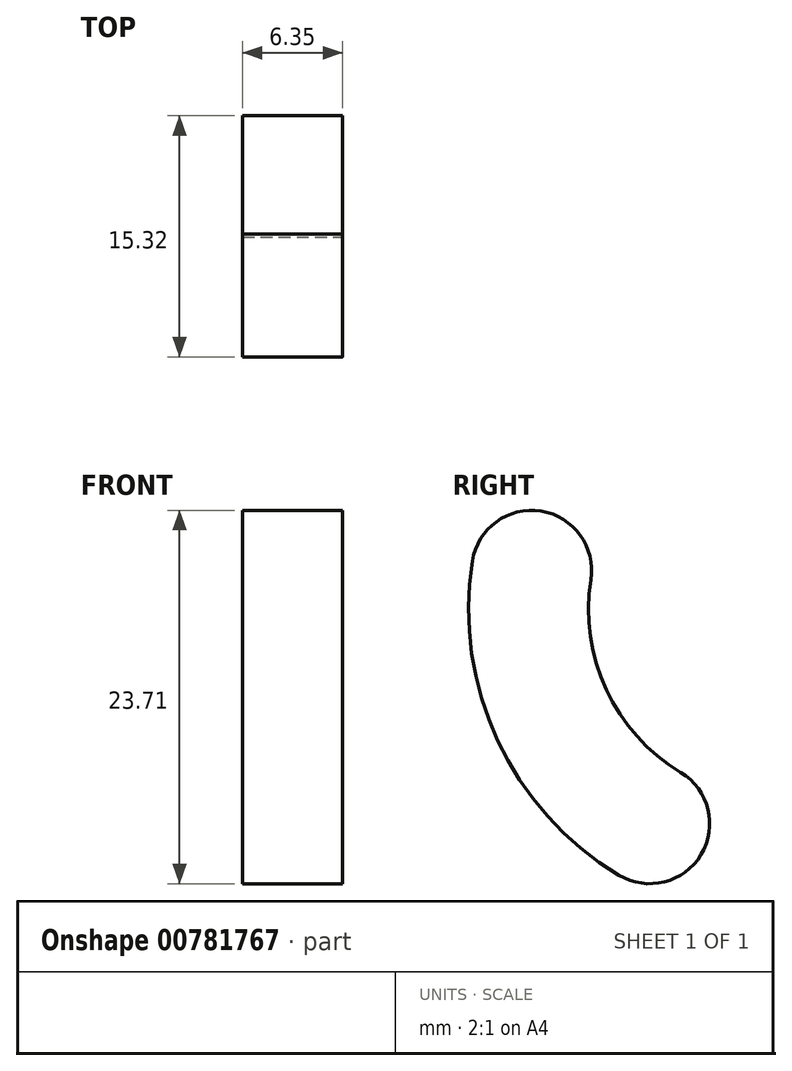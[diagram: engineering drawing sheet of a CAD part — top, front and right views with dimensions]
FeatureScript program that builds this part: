
annotation { "Feature Type Name" : "Feature", "Feature Type Description" : "" }
export const myFeature = defineFeature(function(context is Context, id is Id, definition is map)
    precondition{}
    {
        {
            var Q0;
            Q0=qCreatedBy(makeId("Top.planeOp"),FACE);
            var sketch = newSketch(context, id + "F0", { "sketchPlane" : qUnion([Q0])});
            skLineSegment(sketch, "E0.bottom", {"start": v(31.75, -31.75) * mm, "end": v(-31.75, -31.75) * mm});
            skLineSegment(sketch, "E0.top", {"start": v(31.75, 31.75) * mm, "end": v(-31.75, 31.75) * mm});
            skLineSegment(sketch, "E0.left", {"start": v(31.75, -31.75) * mm, "end": v(31.75, 31.75) * mm});
            skLineSegment(sketch, "E0.right", {"start": v(-31.75, -31.75) * mm, "end": v(-31.75, 31.75) * mm});
            skPoint(sketch, "E0.middle", {"position": v(0, 0) * mm});
            skLineSegment(sketch, "E1.bottom", {"start": v(25.4, -25.4) * mm, "end": v(-25.4, -25.4) * mm});
            skLineSegment(sketch, "E1.top", {"start": v(25.4, 25.4) * mm, "end": v(-25.4, 25.4) * mm});
            skLineSegment(sketch, "E1.left", {"start": v(25.4, -25.4) * mm, "end": v(25.4, 25.4) * mm});
            skLineSegment(sketch, "E1.right", {"start": v(-25.4, -25.4) * mm, "end": v(-25.4, 25.4) * mm});
            skSolve(sketch);
        }
        {
            var Q0;
            Q0=makeQuery(id+"F0.imprint","IMPRINT",FACE,{"disambiguationData":[TD([[makeQuery(id+"F0.imprint","IMPRINT",EDGE,{"derivedFrom":sQuery(id+"F0.wireOp",EDGE,"E0.bottom")}),-1.0]])]});
            extrude(context, id + "F1", {"entities" : qUnion([Q0]), "endBound" : BoundingType.SYMMETRIC, "depth" : 330.2 * mm, "offsetDistance" : 25.4 * mm});
        }
        {
            var Q0;
            Q0=makeQuery(id+"F1.opExtrude","SWEPT_FACE",FACE,{"disambiguationData":[OSD([sQuery(id+"F0.wireOp",EDGE,"E0.right")])]});
            var sketch = newSketch(context, id + "F2", { "sketchPlane" : qUnion([Q0])});
            skSolve(sketch);
        }
        {
            var Q0;
            Q0=makeQuery(id+"F1.opExtrude","SWEPT_FACE",FACE,{"disambiguationData":[OSD([sQuery(id+"F0.wireOp",EDGE,"E0.left")])]});
            var sketch = newSketch(context, id + "F3", { "sketchPlane" : qUnion([Q0])});
            skLineSegment(sketch, "E2.0", {"start": v(-31.75, 165.1) * mm, "end": v(31.75, 165.1) * mm, "construction": true});
            skLineSegment(sketch, "E2.1", {"start": v(-31.75, 165.1) * mm, "end": v(-31.75, -165.1) * mm, "construction": true});
            skLineSegment(sketch, "E2.2", {"start": v(31.75, 165.1) * mm, "end": v(31.75, -165.1) * mm, "construction": true});
            skLineSegment(sketch, "E2.3", {"start": v(-31.75, -165.1) * mm, "end": v(31.75, -165.1) * mm, "construction": true});
            skCircle(sketch, "E3", {"center": v(0, 146.05) * mm, "radius": 6.48 * mm});
            skArc(sketch, "E4", {"start": v(17.84, 137.73) * mm, "mid": v(19.5, 143.31) * mm, "end": v(19.44, 149.13) * mm});
            skArc(sketch, "E5", {"start": v(10.93, 140.95) * mm, "mid": v(11.95, 144.37) * mm, "end": v(11.92, 147.94) * mm});
            skLineSegment(sketch, "E6", {"start": v(0, 146.05) * mm, "end": v(19.44, 149.13) * mm, "construction": true});
            skLineSegment(sketch, "E7", {"start": v(0, 146.05) * mm, "end": v(9.54, 128.83) * mm, "construction": true});
            skLineSegment(sketch, "E8", {"start": v(0, 146.05) * mm, "end": v(24.19, 134.77) * mm, "construction": true});
            skCircle(sketch, "E9", {"center": v(0, 146.05) * mm, "radius": 15.88 * mm, "construction": true});
            skArc(sketch, "E10", {"start": v(11.92, 147.94) * mm, "mid": v(15.08, 152.3) * mm, "end": v(19.44, 149.13) * mm});
            skArc(sketch, "E11.MirrorCS", {"start": v(6.21, 135.7) * mm, "mid": v(4.91, 130.48) * mm, "end": v(10.14, 129.18) * mm});
            skArc(sketch, "E12.MirrorCS", {"start": v(10.93, 140.95) * mm, "mid": v(8.97, 137.98) * mm, "end": v(6.21, 135.7) * mm});
            skArc(sketch, "E13.MirrorCS", {"start": v(17.84, 137.73) * mm, "mid": v(14.63, 132.88) * mm, "end": v(10.14, 129.18) * mm});
            skLineSegment(sketch, "E14", {"start": v(0, 146.05) * mm, "end": v(-19.11, 146.05) * mm, "construction": true});
            skLineSegment(sketch, "E15", {"start": v(0, 146.05) * mm, "end": v(0, 119.4) * mm, "construction": true});
            skArc(sketch, "E16.MirrorCS", {"start": v(-6.21, 135.7) * mm, "mid": v(-4.91, 130.48) * mm, "end": v(-10.14, 129.18) * mm});
            skArc(sketch, "E17.MirrorCS", {"start": v(-17.84, 137.73) * mm, "mid": v(-14.63, 132.88) * mm, "end": v(-10.14, 129.18) * mm});
            skArc(sketch, "E18.MirrorCS", {"start": v(-17.84, 137.73) * mm, "mid": v(-19.5, 143.31) * mm, "end": v(-19.44, 149.13) * mm});
            skArc(sketch, "E19.MirrorCS", {"start": v(-11.92, 147.94) * mm, "mid": v(-15.08, 152.3) * mm, "end": v(-19.44, 149.13) * mm});
            skArc(sketch, "E20.MirrorCS", {"start": v(-10.93, 140.95) * mm, "mid": v(-11.95, 144.37) * mm, "end": v(-11.92, 147.94) * mm});
            skArc(sketch, "E21.MirrorCS", {"start": v(-10.93, 140.95) * mm, "mid": v(-8.97, 137.98) * mm, "end": v(-6.21, 135.7) * mm});
            skSolve(sketch);
        }
        {
            var Q0;
            Q0=makeQuery(id+"F3.imprint","IMPRINT",FACE,{"disambiguationData":[TD([[makeQuery(id+"F3.imprint","IMPRINT",EDGE,{"derivedFrom":sQuery(id+"F3.wireOp",EDGE,"E3")}),1.0]])]});
            var Q1;
            Q1=makeQuery(id+"F3.imprint","IMPRINT",FACE,{"disambiguationData":[TD([[makeQuery(id+"F3.imprint","IMPRINT",EDGE,{"derivedFrom":sQuery(id+"F3.wireOp",EDGE,"E4")}),1.0]])]});
            var Q2;
            Q2=makeQuery(id+"F3.imprint","IMPRINT",FACE,{"disambiguationData":[TD([[makeQuery(id+"F3.imprint","IMPRINT",EDGE,{"derivedFrom":sQuery(id+"F3.wireOp",EDGE,"E16.MirrorCS")}),-1.0]])]});
            extrude(context, id + "F4", {"entities" : qUnion([Q0, Q1, Q2]), "operationType" : NewBodyOperationType.REMOVE, "oppositeDirection" : true, "depth" : 25.4 * mm, "offsetDistance" : 25.4 * mm});
        }
        {
            var Q0;
            {var subQ0=sQuery(id+"F0.wireOp",EDGE,"E0.right");Q0=makeQuery(id+"F2.imprint","IMPRINT",FACE,{"disambiguationData":[TD([[makeQuery(id+"F2.imprint","IMPRINT",EDGE,{"derivedFrom":makeQuery(id+"F1.opExtrude","CAP_EDGE",EDGE,{"disambiguationData":[OSD([subQ0])],"isStart":true})}),-1.0]])]});}
            var sketch = newSketch(context, id + "F5", { "sketchPlane" : qUnion([Q0])});
            skCircle(sketch, "E22.0", {"center": v(0, 146.05) * mm, "radius": 6.48 * mm});
            skCircle(sketch, "E23", {"center": v(-7.7, 132.17) * mm, "radius": 1.9 * mm});
            skArc(sketch, "E24", {"start": v(5.1, 127.04) * mm, "mid": v(17.84, 137.73) * mm, "end": v(17.84, 154.37) * mm});
            skCircle(sketch, "E25", {"center": v(0, 146.05) * mm, "radius": 15.88 * mm, "construction": true});
            skLineSegment(sketch, "E26", {"start": v(0, 146.05) * mm, "end": v(5.1, 127.04) * mm, "construction": true});
            skLineSegment(sketch, "E27", {"start": v(0, 146.05) * mm, "end": v(-15.88, 146.05) * mm, "construction": true});
            skLineSegment(sketch, "E28", {"start": v(0, 146.05) * mm, "end": v(17.84, 154.37) * mm, "construction": true});
            skArc(sketch, "E29", {"start": v(3.12, 134.4) * mm, "mid": v(10.93, 140.95) * mm, "end": v(10.93, 151.15) * mm});
            skLineSegment(sketch, "E30", {"start": v(0, 146.05) * mm, "end": v(-7.7, 132.17) * mm});
            skArc(sketch, "E31", {"start": v(3.12, 134.4) * mm, "mid": v(0.43, 129.73) * mm, "end": v(5.1, 127.04) * mm});
            skArc(sketch, "E32", {"start": v(17.84, 154.37) * mm, "mid": v(12.78, 156.21) * mm, "end": v(10.93, 151.15) * mm});
            skCircle(sketch, "E33", {"center": v(-7.7, 132.17) * mm, "radius": 3.18 * mm, "construction": true});
            skLineSegment(sketch, "E34", {"start": v(0, 146.05) * mm, "end": v(-15.58, 149.08) * mm, "construction": true});
            skCircle(sketch, "E35", {"center": v(-15.58, 149.08) * mm, "radius": 3.18 * mm, "construction": true});
            skArc(sketch, "E36.0", {"start": v(-11.92, 147.94) * mm, "mid": v(-15.08, 152.3) * mm, "end": v(-19.44, 149.13) * mm, "construction": true});
            skLineSegment(sketch, "E37", {"start": v(0, 146.05) * mm, "end": v(-15.68, 148.53) * mm, "construction": true});
            skSolve(sketch);
        }
        {
            var Q0;
            Q0=qSketchRegion(id+"F5",true);
            extrude(context, id + "F6", {"entities" : qUnion([Q0]), "operationType" : NewBodyOperationType.REMOVE, "oppositeDirection" : true, "depth" : 25.4 * mm, "offsetDistance" : 25.4 * mm});
        }
        {
            var Q0;
            Q0=makeQuery(id+"F1.opExtrude","SWEPT_FACE",FACE,{"disambiguationData":[OSD([sQuery(id+"F0.wireOp",EDGE,"E0.left")])]});
            var sketch = newSketch(context, id + "F7", { "sketchPlane" : qUnion([Q0])});
            skArc(sketch, "E38", {"start": v(-8.89, 101.6) * mm, "mid": v(10.16, 82.55) * mm, "end": v(-8.89, 63.5) * mm, "construction": true});
            skArc(sketch, "E39.0", {"start": v(-8.89, 95.25) * mm, "mid": v(3.81, 82.55) * mm, "end": v(-8.89, 69.85) * mm});
            skArc(sketch, "E40.0", {"start": v(-8.89, 107.95) * mm, "mid": v(16.5, 82.55) * mm, "end": v(-8.89, 57.15) * mm});
            skArc(sketch, "E41", {"start": v(-8.89, 107.95) * mm, "mid": v(-15.24, 101.6) * mm, "end": v(-8.89, 95.25) * mm});
            skArc(sketch, "E42", {"start": v(-8.89, 57.15) * mm, "mid": v(-15.24, 63.5) * mm, "end": v(-8.89, 69.85) * mm});
            skArc(sketch, "E43", {"start": v(8.9, 6.35) * mm, "mid": v(-10.16, 25.4) * mm, "end": v(8.9, 44.45) * mm, "construction": true});
            skArc(sketch, "E44.0", {"start": v(8.9, 12.7) * mm, "mid": v(-3.8, 25.4) * mm, "end": v(8.9, 38.1) * mm});
            skArc(sketch, "E45.0", {"start": v(8.9, 0) * mm, "mid": v(-16.5, 25.4) * mm, "end": v(8.89, 50.8) * mm});
            skArc(sketch, "E46", {"start": v(8.9, 0) * mm, "mid": v(15.24, 6.35) * mm, "end": v(8.9, 12.7) * mm});
            skArc(sketch, "E47", {"start": v(8.9, 50.8) * mm, "mid": v(15.24, 44.45) * mm, "end": v(8.9, 38.1) * mm});
            skArc(sketch, "E48", {"start": v(-8.89, -12.7) * mm, "mid": v(10.16, -31.75) * mm, "end": v(-8.89, -50.8) * mm, "construction": true});
            skArc(sketch, "E49.0", {"start": v(-8.89, -19.05) * mm, "mid": v(3.81, -31.75) * mm, "end": v(-8.89, -44.45) * mm});
            skArc(sketch, "E50.0", {"start": v(-8.89, -6.35) * mm, "mid": v(16.5, -31.75) * mm, "end": v(-8.89, -57.15) * mm});
            skArc(sketch, "E51", {"start": v(-8.89, -6.35) * mm, "mid": v(-15.24, -12.7) * mm, "end": v(-8.89, -19.05) * mm});
            skArc(sketch, "E52", {"start": v(-8.89, -57.15) * mm, "mid": v(-15.24, -50.8) * mm, "end": v(-8.89, -44.45) * mm});
            skArc(sketch, "E53", {"start": v(8.9, -107.95) * mm, "mid": v(-10.16, -88.9) * mm, "end": v(8.89, -69.85) * mm, "construction": true});
            skArc(sketch, "E54.0", {"start": v(8.9, -101.6) * mm, "mid": v(-3.8, -88.9) * mm, "end": v(8.89, -76.2) * mm});
            skArc(sketch, "E55.0", {"start": v(8.9, -114.3) * mm, "mid": v(-16.5, -88.9) * mm, "end": v(8.89, -63.5) * mm});
            skArc(sketch, "E56", {"start": v(8.9, -114.3) * mm, "mid": v(15.24, -107.95) * mm, "end": v(8.9, -101.6) * mm});
            skArc(sketch, "E57", {"start": v(8.89, -63.5) * mm, "mid": v(15.24, -69.85) * mm, "end": v(8.89, -76.2) * mm});
            skCircle(sketch, "E58", {"center": v(-8.89, 82.55) * mm, "radius": 6.35 * mm});
            skCircle(sketch, "E59", {"center": v(8.9, 25.4) * mm, "radius": 6.35 * mm});
            skCircle(sketch, "E60", {"center": v(8.9, -88.9) * mm, "radius": 6.35 * mm});
            skCircle(sketch, "E61", {"center": v(-8.89, -31.75) * mm, "radius": 6.35 * mm});
            skSolve(sketch);
        }
        {
            var Q0;
            Q0=qSketchRegion(id+"F7",true);
            extrude(context, id + "F8", {"entities" : qUnion([Q0]), "operationType" : NewBodyOperationType.REMOVE, "endBound" : BoundingType.THROUGH_ALL, "oppositeDirection" : true, "depth" : 25.4 * mm, "offsetDistance" : 25.4 * mm});
        }
        {
            var Q0;
            Q0=makeQuery(id+"F1.opExtrude","SWEPT_FACE",FACE,{"disambiguationData":[OSD([sQuery(id+"F0.wireOp",EDGE,"E1.left")])]});
            var sketch = newSketch(context, id + "F9", { "sketchPlane" : qUnion([Q0])});
            skLineSegment(sketch, "E62.bottom", {"start": v(-25.4, 165.1) * mm, "end": v(25.4, 165.1) * mm});
            skLineSegment(sketch, "E62.top", {"start": v(-25.4, -127) * mm, "end": v(25.4, -127) * mm});
            skLineSegment(sketch, "E62.left", {"start": v(-25.4, 165.1) * mm, "end": v(-25.4, -127) * mm});
            skLineSegment(sketch, "E62.right", {"start": v(25.4, 165.1) * mm, "end": v(25.4, -127) * mm});
            skLineSegment(sketch, "E63.bottom", {"start": v(46.54, -190) * mm, "end": v(-46.54, -190) * mm});
            skLineSegment(sketch, "E63.top", {"start": v(46.54, 190) * mm, "end": v(-46.54, 190) * mm});
            skLineSegment(sketch, "E63.left", {"start": v(46.54, -190) * mm, "end": v(46.54, 190) * mm});
            skLineSegment(sketch, "E63.right", {"start": v(-46.54, -190) * mm, "end": v(-46.54, 190) * mm});
            skPoint(sketch, "E63.middle", {"position": v(0, 0) * mm});
            skSolve(sketch);
        }
        {
            var Q0;
            Q0 = qSketchRegion(id + "F9", true);
            extrude(context, id + "F10", {"entities" : qUnion([Q0]), "operationType" : NewBodyOperationType.REMOVE, "endBound" : BoundingType.SYMMETRIC, "oppositeDirection" : true, "depth" : 76.2 * mm, "offsetDistance" : 25.4 * mm});
        }
        {
            var Q0;
            Q0=makeQuery(id+"F1.opExtrude","SWEPT_FACE",FACE,{"disambiguationData":[OSD([sQuery(id+"F0.wireOp",EDGE,"E1.left")])]});
            var sketch = newSketch(context, id + "F11", { "sketchPlane" : qUnion([Q0])});
            skLineSegment(sketch, "E64.bottom", {"start": v(46.98, -190.95) * mm, "end": v(-46.98, -190.95) * mm});
            skLineSegment(sketch, "E64.top", {"start": v(46.98, 190.95) * mm, "end": v(-46.98, 190.95) * mm});
            skLineSegment(sketch, "E64.left", {"start": v(46.98, -190.95) * mm, "end": v(46.98, 190.95) * mm});
            skLineSegment(sketch, "E64.right", {"start": v(-46.98, -190.95) * mm, "end": v(-46.98, 190.95) * mm});
            skPoint(sketch, "E64.middle", {"position": v(0, 0) * mm});
            skSolve(sketch);
        }
        {
            var Q0;
            Q0 = qSketchRegion(id + "F11", true);
            extrude(context, id + "F12", {"entities" : qUnion([Q0]), "operationType" : NewBodyOperationType.REMOVE, "depth" : 91.44 * mm, "offsetDistance" : 25.4 * mm});
        }
    });
